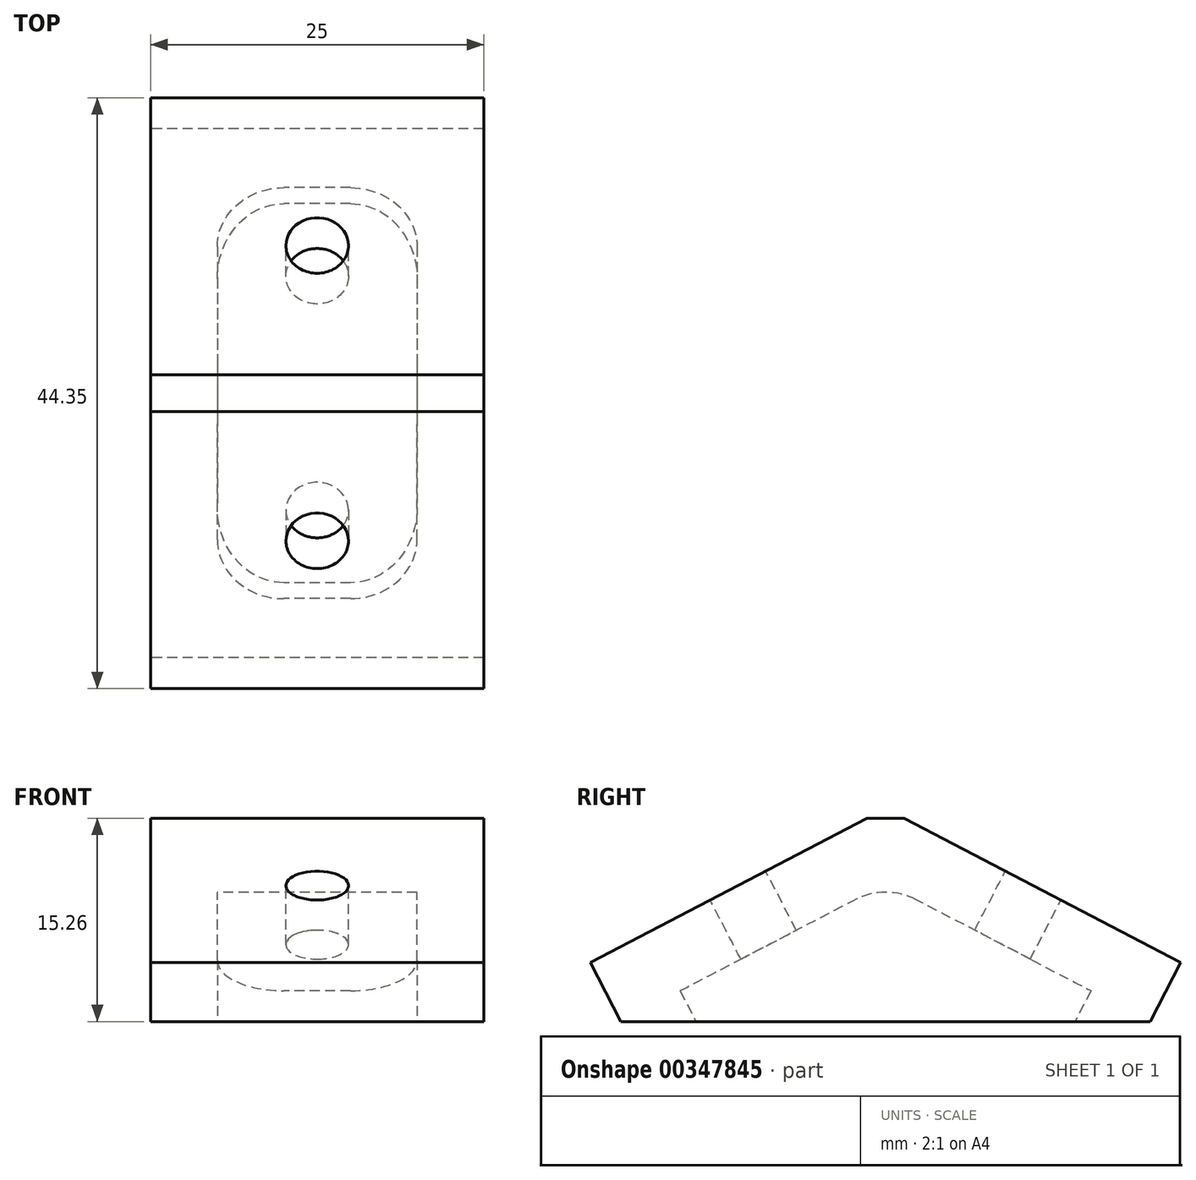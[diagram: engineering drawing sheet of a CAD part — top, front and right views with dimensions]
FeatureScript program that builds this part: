
annotation { "Feature Type Name" : "Feature", "Feature Type Description" : "" }
export const myFeature = defineFeature(function(context is Context, id is Id, definition is map)
    precondition{}
    {
        {
            var Q0;
            Q0=qCreatedBy(makeId("Right.planeOp"),FACE);
            var sketch = newSketch(context, id + "F0", { "sketchPlane" : qUnion([Q0])});
            skLineSegment(sketch, "E0", {"start": v(0, -25) * mm, "end": v(0, 0) * mm});
            skLineSegment(sketch, "E1", {"start": v(20.48, 14.34) * mm, "end": v(0, 0) * mm});
            skLineSegment(sketch, "E2", {"start": v(20.48, 14.34) * mm, "end": v(0, -25) * mm, "construction": true});
            skLineSegment(sketch, "E3.0", {"start": v(23.35, 10.24) * mm, "end": v(5, -2.6) * mm});
            skLineSegment(sketch, "E3.1", {"start": v(5, -25) * mm, "end": v(5, -2.6) * mm});
            skLineSegment(sketch, "E4", {"start": v(0, -25) * mm, "end": v(5, -25) * mm});
            skLineSegment(sketch, "E5", {"start": v(20.48, 14.34) * mm, "end": v(23.35, 10.24) * mm});
            skLineSegment(sketch, "E6", {"start": v(23.35, 10.24) * mm, "end": v(5, -25) * mm});
            skSolve(sketch);
        }
        {
            var Q0;
            Q0=qSketchRegion(id+"F0",true);
            extrude(context, id + "F1", {"entities" : qUnion([Q0]), "depth" : 25 * mm});
        }
        {
            var Q0;
            Q0=makeQuery(id+"F1.opExtrude","SWEPT_FACE",FACE,{"disambiguationData":[OSD([sQuery(id+"F0.wireOp",EDGE,"E6")])]});
            shell(context, id + "F2", {"entities" : qUnion([Q0]), "thickness" : 5 * mm});
        }
        {
            var Q0;
            {var subQ0=sQuery(id+"F0.wireOp",EDGE,"E5");Q0=makeQuery(id+"F2.opShell","OFFSET_EDGE",EDGE,{"disambiguationData":[OSD([subQ0]),TDD([makeQuery(id+"F1.opExtrude","CAP_EDGE",EDGE,{"disambiguationData":[OSD([subQ0])],"isStart":false})])]});}
            var Q1;
            {var subQ0=sQuery(id+"F0.wireOp",EDGE,"E5");Q1=makeQuery(id+"F2.opShell","OFFSET_EDGE",EDGE,{"disambiguationData":[OSD([subQ0]),TDD([makeQuery(id+"F1.opExtrude","CAP_EDGE",EDGE,{"disambiguationData":[OSD([subQ0])],"isStart":true})])]});}
            var Q2;
            {var subQ0=sQuery(id+"F0.wireOp",EDGE,"E4");Q2=makeQuery(id+"F2.opShell","OFFSET_EDGE",EDGE,{"disambiguationData":[OSD([subQ0]),TDD([makeQuery(id+"F1.opExtrude","CAP_EDGE",EDGE,{"disambiguationData":[OSD([subQ0])],"isStart":false})])]});}
            var Q3;
            {var subQ0=sQuery(id+"F0.wireOp",EDGE,"E4");Q3=makeQuery(id+"F2.opShell","OFFSET_EDGE",EDGE,{"disambiguationData":[OSD([subQ0]),TDD([makeQuery(id+"F1.opExtrude","CAP_EDGE",EDGE,{"disambiguationData":[OSD([subQ0])],"isStart":true})])]});}
            fillet(context, id + "F3", {"entities" : qUnion([Q0, Q1, Q2, Q3]), "radius" : 5 * mm, "tangentPropagation" : true, "allowEdgeOverflow" : false});
        }
        {
            var Q0;
            Q0=makeQuery(id+"F2.opShell","OFFSET_EDGE",EDGE,{"disambiguationData":[OSD([sQuery(id+"F0.wireOp",EDGE,"E0"),sQuery(id+"F0.wireOp",EDGE,"E1")])]});
            fillet(context, id + "F4", {"entities" : qUnion([Q0]), "radius" : 5 * mm, "tangentPropagation" : true, "allowEdgeOverflow" : false});
        }
        {
            var Q0;
            Q0=makeQuery(id+"F1.opExtrude","SWEPT_EDGE",EDGE,{"disambiguationData":[OSD([sQuery(id+"F0.wireOp",EDGE,"E0"),sQuery(id+"F0.wireOp",EDGE,"E1")])]});
            chamfer(context, id + "F5", {"entities" : qUnion([Q0]), "width" : 3 * mm, "tangentPropagation" : true});
        }
        {
            var Q0;
            Q0=makeQuery(id+"F1.opExtrude","SWEPT_FACE",FACE,{"disambiguationData":[OSD([sQuery(id+"F0.wireOp",EDGE,"E1")])]});
            var sketch = newSketch(context, id + "F6", { "sketchPlane" : qUnion([Q0])});
            skCircle(sketch, "E7", {"center": v(12.5, 12.5) * mm, "radius": 2.35 * mm});
            skLineSegment(sketch, "E8.0", {"start": v(0, 25) * mm, "end": v(0, 3) * mm, "construction": true});
            skLineSegment(sketch, "E9.0", {"start": v(0, 3) * mm, "end": v(25, 3) * mm, "construction": true});
            skLineSegment(sketch, "E10.0", {"start": v(25, 25) * mm, "end": v(0, 25) * mm, "construction": true});
            skLineSegment(sketch, "E11.0", {"start": v(25, 25) * mm, "end": v(25, 3) * mm, "construction": true});
            skSolve(sketch);
        }
        {
            var Q0;
            Q0=makeQuery(id+"F6.imprint","IMPRINT",FACE,{"disambiguationData":[TD([[makeQuery(id+"F6.imprint","IMPRINT",EDGE,{"derivedFrom":sQuery(id+"F6.wireOp",EDGE,"E7")}),1.0]])]});
            extrude(context, id + "F7", {"entities" : qUnion([Q0]), "operationType" : NewBodyOperationType.REMOVE, "oppositeDirection" : true, "depth" : 25 * mm});
        }
        {
            var Q0;
            Q0=makeQuery(id+"F1.opExtrude","SWEPT_FACE",FACE,{"disambiguationData":[OSD([sQuery(id+"F0.wireOp",EDGE,"E0")])]});
            var sketch = newSketch(context, id + "F8", { "sketchPlane" : qUnion([Q0])});
            skLineSegment(sketch, "E12.0", {"start": v(0, -25) * mm, "end": v(0, -3) * mm, "construction": true});
            skLineSegment(sketch, "E13.0", {"start": v(25, -25) * mm, "end": v(0, -25) * mm, "construction": true});
            skCircle(sketch, "E14", {"center": v(12.5, -12.5) * mm, "radius": 2.35 * mm});
            skSolve(sketch);
        }
        {
            var Q0;
            Q0=qSketchRegion(id+"F8",true);
            extrude(context, id + "F9", {"entities" : qUnion([Q0]), "operationType" : NewBodyOperationType.REMOVE, "oppositeDirection" : true, "depth" : 25 * mm});
        }
        {
            var Q0;
            Q0=makeQuery(id+"F1.opExtrude","SWEPT_BODY",BODY,{"disambiguationData":[OSD([sQuery(id+"F0.wireOp",EDGE,"E0"),sQuery(id+"F0.wireOp",EDGE,"E1"),sQuery(id+"F0.wireOp",EDGE,"E4"),sQuery(id+"F0.wireOp",EDGE,"E5"),sQuery(id+"F0.wireOp",EDGE,"E6")])]});
            var Q1;
            {var subQ0=sQuery(id+"F0.wireOp",EDGE,"E0");Q1=makeQuery(id+"F5.opChamfer","BLEND_EDGE",EDGE,{"blendedFrom":[makeQuery(id+"F1.opExtrude","SWEPT_EDGE",EDGE,{"disambiguationData":[OSD([subQ0,sQuery(id+"F0.wireOp",EDGE,"E1")])]}),makeQuery(id+"F1.opExtrude","SWEPT_FACE",FACE,{"disambiguationData":[OSD([subQ0])]})],"blendedInto":[makeQuery(id+"F1.opExtrude","SWEPT_FACE",FACE,{"disambiguationData":[OSD([subQ0])]})]});}
            transform(context, id + "F10", {"entities" : qUnion([Q0]), "transformType" : TransformType.ROTATION, "transformAxis" : qUnion([Q1]), "angle" : 297.5 * degree, "oppositeDirection" : true, "makeCopy" : false});
        }
        {
            var Q0;
            Q0=makeQuery(id+"F1.opExtrude","SWEPT_BODY",BODY,{"disambiguationData":[OSD([sQuery(id+"F0.wireOp",EDGE,"E0"),sQuery(id+"F0.wireOp",EDGE,"E1"),sQuery(id+"F0.wireOp",EDGE,"E4"),sQuery(id+"F0.wireOp",EDGE,"E5"),sQuery(id+"F0.wireOp",EDGE,"E6")])]});
            var Q1;
            Q1=qCreatedBy(makeId("Top.planeOp"),FACE);
            transform(context, id + "F11", {"entities" : qUnion([Q0]), "transformType" : TransformType.TRANSLATION_DISTANCE, "transformDirection" : qUnion([Q1]), "distance" : 17.6 * mm, "makeCopy" : false});
        }
    });
